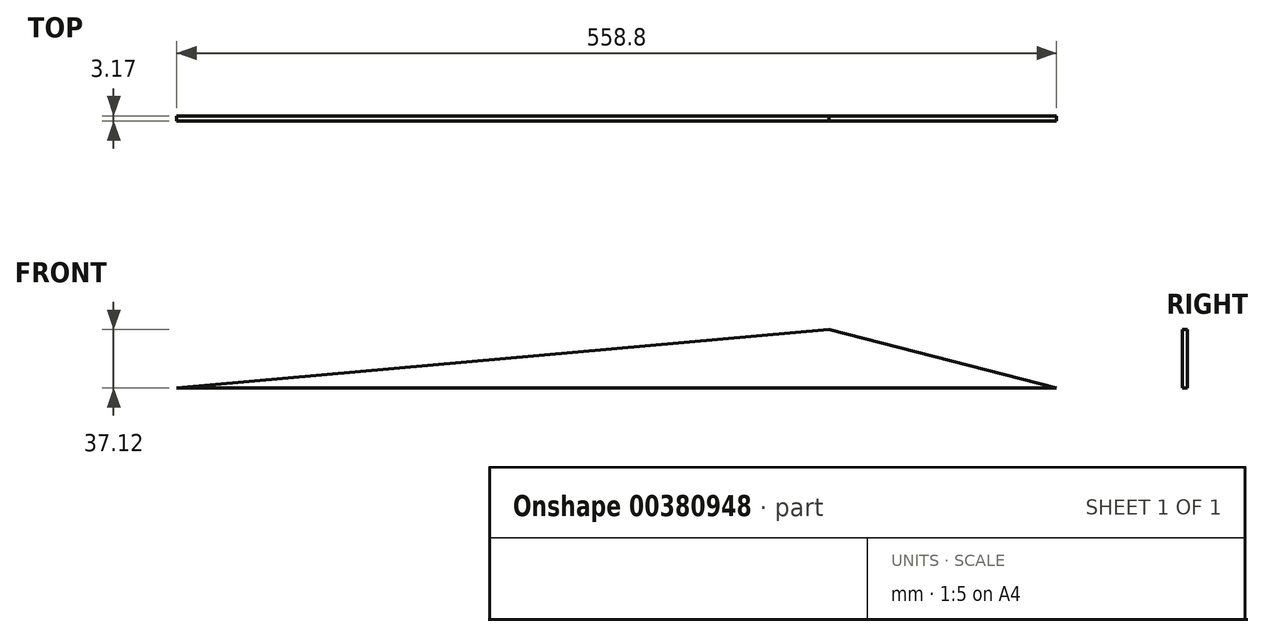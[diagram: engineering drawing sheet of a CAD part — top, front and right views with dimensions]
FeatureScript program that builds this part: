
annotation { "Feature Type Name" : "Feature", "Feature Type Description" : "" }
export const myFeature = defineFeature(function(context is Context, id is Id, definition is map)
    precondition{}
    {
        {
            var Q0;
            Q0=qCreatedBy(makeId("Front.planeOp"),FACE);
            var sketch = newSketch(context, id + "F0", { "sketchPlane" : qUnion([Q0])});
            skLineSegment(sketch, "E0", {"start": v(-281.9, 0) * mm, "end": v(276.9, 0) * mm});
            skLineSegment(sketch, "E1", {"start": v(276.9, 0) * mm, "end": v(132.36, 37.12) * mm});
            skLineSegment(sketch, "E2", {"start": v(132.36, 37.12) * mm, "end": v(-281.9, 0) * mm});
            skSolve(sketch);
        }
        {
            var Q0;
            Q0=qSketchRegion(id+"F0",true);
            extrude(context, id + "F1", {"entities" : qUnion([Q0]), "depth" : 3.17 * mm});
        }
    });
